# Revit family: Haworth_Luxor_Cabinet_10
name_source: partatom
category: Furniture
revit_build: Autodesk Revit 2018 (Build: 20170223_1515(x64)
units: mm (PartAtom-declared; Revit-internal decimal feet)

## family parameters
Always vertical = Yes
Cut with Voids When Loaded = No
OmniClass Number = 23.40.20.00
OmniClass Title = General Furniture and Specialties
Room Calculation Point = No
Shared = No
Work Plane-Based = No

## types (4) — shared parameters
Actual Depth = 1' - 5 3/4"
Assembly Code = E2020200
Manufacturer = Haworth
Model = HCCE-LX
Size = Verify Final Dim. w/ Haworth
URL = http://www.haworth.com
URL - Product = https://www.haworth.com
Version = 3
Warranty = http://www.haworth.com

## per-type parameters (varying)
| type | Actual Height | Actual Width | Cabinet | Console | Description | Drawer Height | Drawer Qty | Drawer Start Location | Drawer Width | Three Drawers | Top Height | Two Drawers |
| HCCE-LX - Two Drawers - 71w 28h | 2' - 4 1/4" | 5' - 10 3/4" | No | Yes | Haworth Luxor Cabinet 10 - Two Drawers - 71w 28h | 0' - 4 3/16" | 2 | 1' - 5 21/32" | 2' - 11 5/16" | No | 0' - 4 3/16" | Yes |
| HCCE-LX - Three Drawers - 106w 28h | 2' - 4 1/4" | 8' - 10 1/4" | No | Yes | Haworth Luxor Cabinet 10 - Three Drawers - 106w 28h | 0' - 4 3/16" | 3 | 1' - 5 11/16" | 2' - 11 3/8" | Yes | 0' - 4 3/16" | No |
| HCCE-LX - Two Drawers - 71w 16h | 1' - 4 1/2" | 5' - 10 3/4" | Yes | No | Haworth Luxor Cabinet 10 - Two Drawers - 71w 16h | 0' - 10" | 2 | 1' - 5 21/32" | 2' - 11 5/16" | No | 0' - 10" | Yes |
| HCCE-LX - Three Drawers - 106w 16h | 1' - 4 1/2" | 8' - 10 1/4" | Yes | No | Haworth Luxor Cabinet 10 - Three Drawers - 106w 16h | 0' - 10" | 3 | 1' - 5 11/16" | 2' - 11 3/8" | Yes | 0' - 10" | No |

## geometry (parser evidence)
native form markers: Blend x4, Sweep x7
no freeform markers — native parametric forms only
